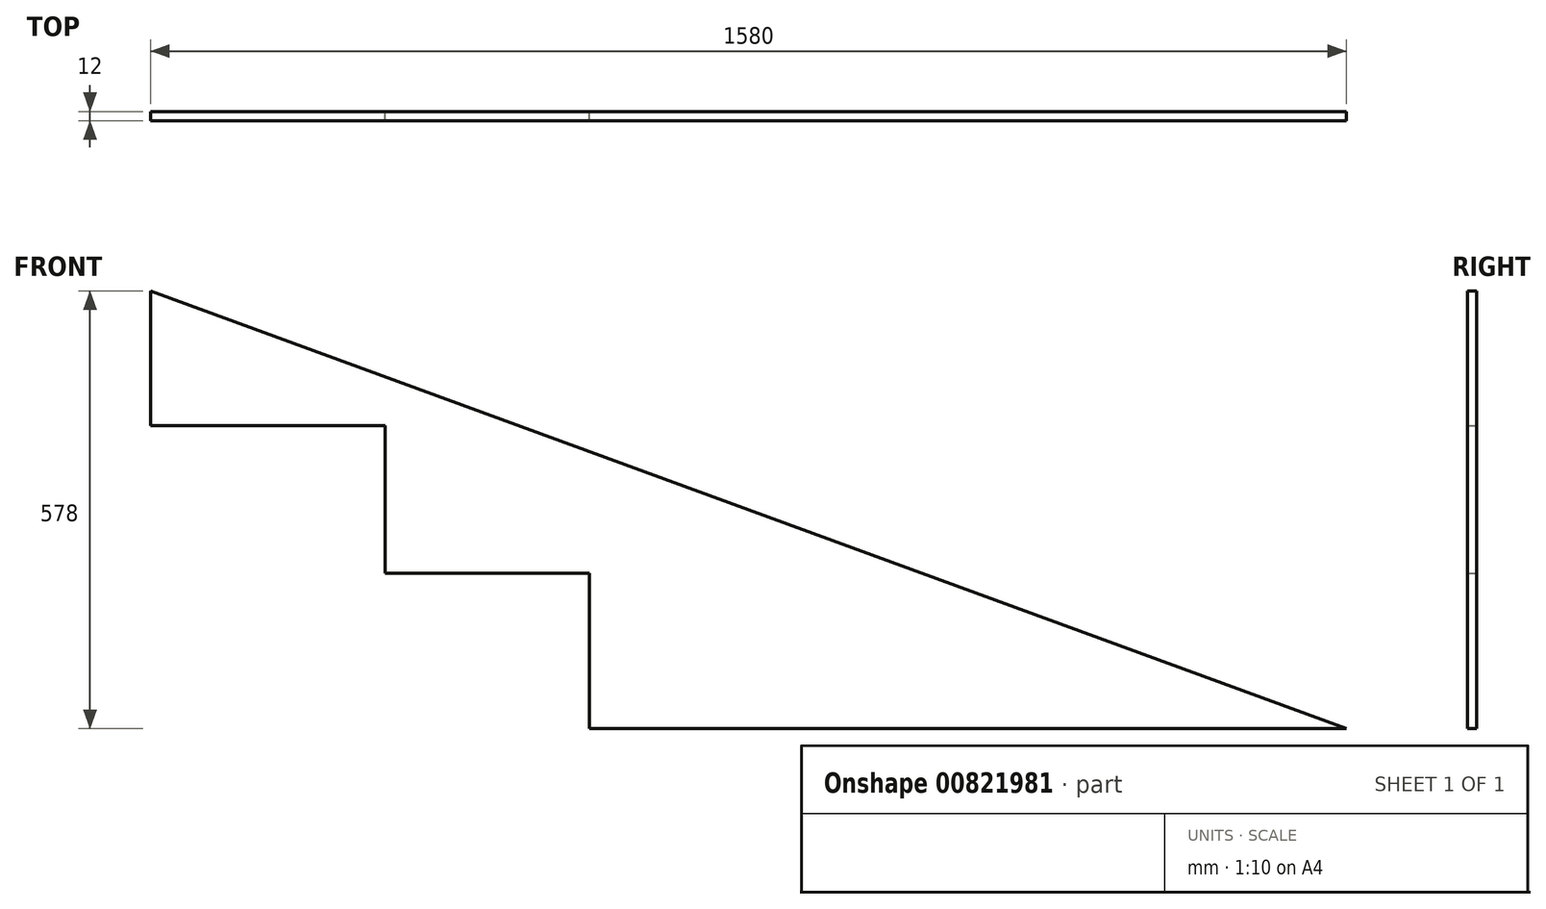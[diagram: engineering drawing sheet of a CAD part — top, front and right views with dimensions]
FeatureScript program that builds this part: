
annotation { "Feature Type Name" : "Feature", "Feature Type Description" : "" }
export const myFeature = defineFeature(function(context is Context, id is Id, definition is map)
    precondition{}
    {
        {
            var Q0;
            Q0=qCreatedBy(makeId("Front.planeOp"),FACE);
            var sketch = newSketch(context, id + "F0", { "sketchPlane" : qUnion([Q0])});
            skLineSegment(sketch, "E0", {"start": v(-62.58, 129) * mm, "end": v(-62.58, -49) * mm});
            skLineSegment(sketch, "E1", {"start": v(-62.58, -49) * mm, "end": v(247.42, -49) * mm});
            skLineSegment(sketch, "E2", {"start": v(247.42, -49) * mm, "end": v(247.42, -244) * mm});
            skLineSegment(sketch, "E3", {"start": v(247.42, -244) * mm, "end": v(517.42, -244) * mm});
            skLineSegment(sketch, "E4", {"start": v(517.42, -244) * mm, "end": v(517.42, -449) * mm});
            skLineSegment(sketch, "E5", {"start": v(517.42, -449) * mm, "end": v(1517.42, -449) * mm});
            skLineSegment(sketch, "E6", {"start": v(1517.42, -449) * mm, "end": v(-62.58, 129) * mm});
            skSolve(sketch);
        }
        {
            var Q0;
            Q0=makeQuery(id+"F0.imprint","IMPRINT",FACE,{"disambiguationData":[TD([[makeQuery(id+"F0.imprint","IMPRINT",EDGE,{"derivedFrom":sQuery(id+"F0.wireOp",EDGE,"E0")}),1.0]])]});
            extrude(context, id + "F1", {"entities" : qUnion([Q0]), "depth" : 12 * mm, "offsetDistance" : 25 * mm});
        }
    });
